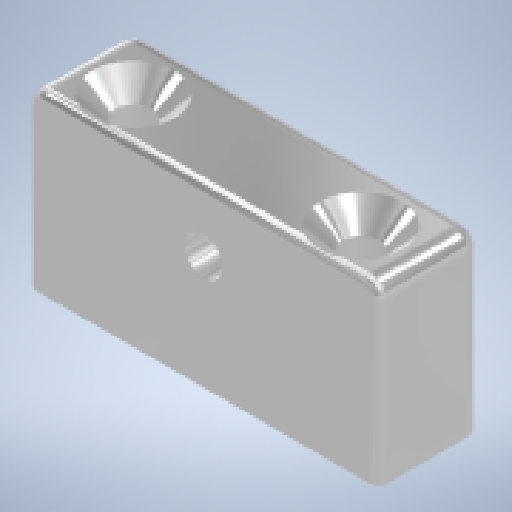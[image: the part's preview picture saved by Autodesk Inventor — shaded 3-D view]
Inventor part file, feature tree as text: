
AUTODESK INVENTOR PART (.ipt)
format: ipt  version: 2025 (Build 290162010, 162A)  size: 198,144 bytes
history: native  units: mm
features: sketch x3, hole x2, fillet x2, extrude x1
ambient origin geometry x8: Origin, YZ Plane, XZ Plane, XY Plane, X Axis, Y Axis, Z Axis, Center Point
bodies: Volumenkörper1 (feature_tree)
feature tree (8):
  extrude  "Extrusion1"  Depth=12.0mm
  hole  "Bohrung1"  [1 undecoded]
  hole  "Bohrung5"  [1 undecoded]
  fillet  "Rundung3"  Radius=7.0mm
  fillet  "Rundung4"  Radius=2.0mm
  sketch  "Skizze1"  dims[d0=40.0mm d1=12.0mm]
  sketch  "Skizze2"  dims[d2=20.0mm d3=0.0mm d4=7.0mm]
  sketch  "Skizze4"  dims[d5=4.3mm d6=6.0mm d7=9.4mm d8=4.0mm d9=90.0deg d10=15.0mm d11=20.594885mm d12=7.0mm d37=7.0mm d38=4.3mm d39=8.0mm d40=9.4mm d41=2.0mm d42=90.0deg d43=10.0mm d44=20.594885mm d45=2.0mm d46=1.0mm d29=1.0mm d30=1.0mm d31=1.0mm d32=0.15mm d33=0.25mm d34=0.375mm d35=14.3117mm d36=0.75mm]
note: 2 required parameter values undecoded (feature->parameter linkage not recoverable at this tier; creation-order binding heuristic only, values carry confidence <= 0.55)
